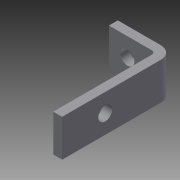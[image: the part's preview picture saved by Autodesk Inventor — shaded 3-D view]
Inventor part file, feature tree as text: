
AUTODESK INVENTOR PART (.ipt)
format: ipt  version: 2013 (Build 170138000, 138)  size: 108,032 bytes
history: native  units: in
note: dims shown in document units (in); Inventor stores cm internally (conversion verified against a paired STEP export)
features: sheet_metal_op x4, sketch x3, other x2, extrude x1
ambient origin geometry x8: Origin, YZ Plane, XZ Plane, XY Plane, X Axis, Y Axis, Z Axis, Center Point
bodies: Solid1 (feature_tree)
feature tree (10):
  sheet_metal_op  "Face1"
  sheet_metal_op  "Flange1"
  extrude  "Extrusion1"  Depth=0.25in
  sketch  "Sketch1"  dims[d0=0.188in d1=0.25in]
  other  "Plate1"
  sketch  "Sketch2"  dims[d4=0.5in]
  other  "Plate2"
  sheet_metal_op  "Bend1"
  sheet_metal_op  "Corner1"
  sketch  "Sketch3"  dims[d6=0.12in d7=0.12in d8=0.06in d9=0.24in d10=0.12in d11=1.5in d12=90.0deg d13=0.05in d14=0.48in d15=0.12in d16=0.12in d17=0.1875in d18=1.0in d19=0.0in d20=0.25in d21=0.75in d22=0.75in d23=0.5in]
